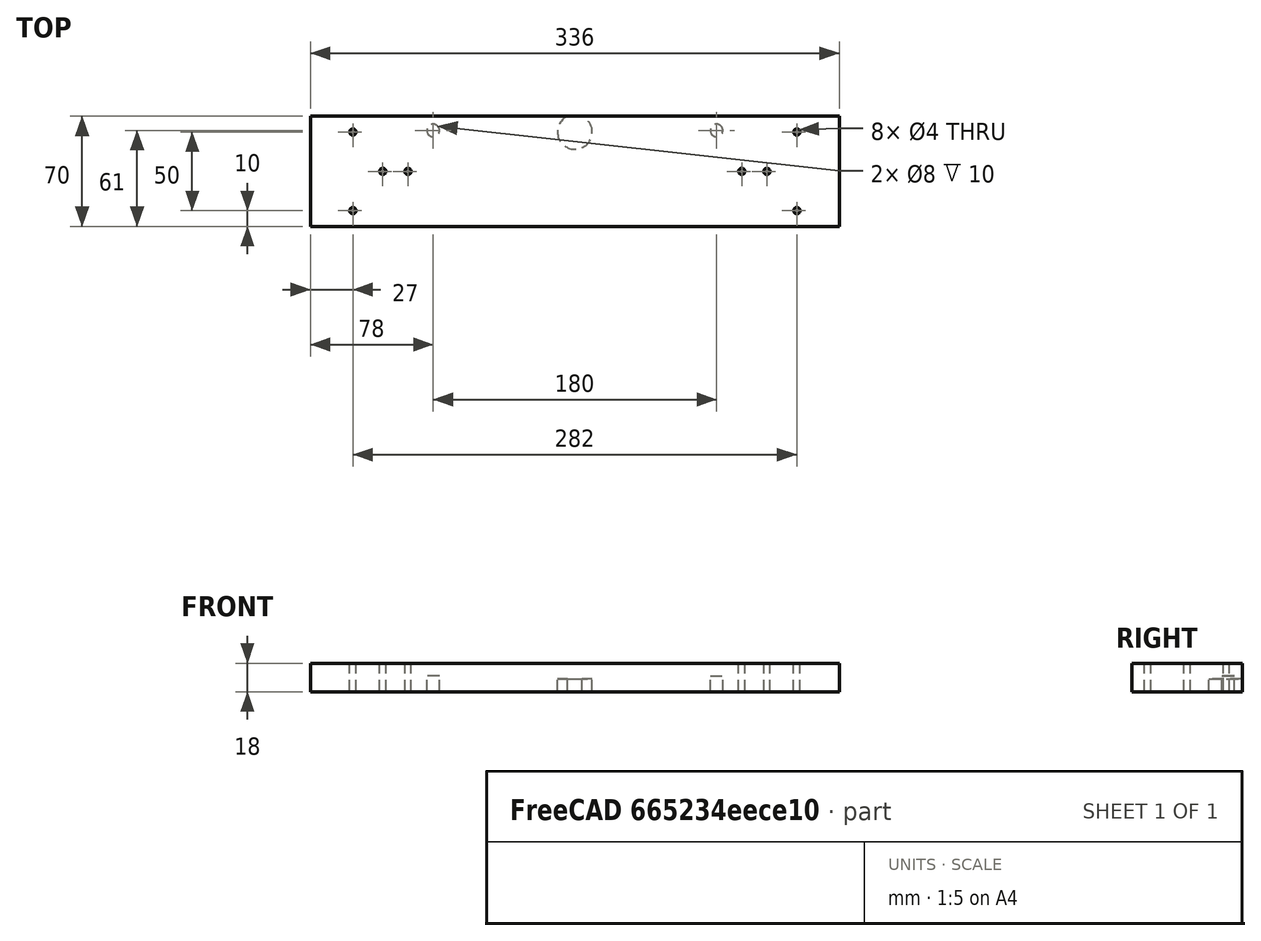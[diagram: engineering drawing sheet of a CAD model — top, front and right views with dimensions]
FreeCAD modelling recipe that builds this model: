
FCSTD DOCUMENT  (FreeCAD 0.17R13541 (Git))
Label: Base-Atras
License: All rights reserved
LicenseURL: http://en.wikipedia.org/wiki/All_rights_reserved
objects: Part::Cylinder×6, Part::MultiFuse×2, Part::Cut×2, Part::Box×1, Part::Mirroring×1
note: 12 computed .brp shape members not serialized (recipe doc carries the construction recipe); baked Part::Feature solids carry a one-line shape summary decoded from their .brp

FEATURE [Part::Box] Box  label="Base"
  AttacherType = Attacher::AttachEngine3D
  Height = 18
  Length = 168
  Width = 70
FEATURE [Part::Cylinder] Cylinder  label="Cilindro"
  Angle = 360
  AttacherType = Attacher::AttachEngine3D
  Height = 25
  Placement = pos=(27,10,0) rot=(0,0,1;0rad)
  Radius = 2
FEATURE [Part::Cylinder] Cylinder001  label="Cilindro001"
  Angle = 360
  AttacherType = Attacher::AttachEngine3D
  Height = 25
  Placement = pos=(27,60,0) rot=(0,0,1;0rad)
  Radius = 2
FEATURE [Part::Cylinder] Cylinder002  label="Cilindro002"
  Angle = 360
  AttacherType = Attacher::AttachEngine3D
  Height = 25
  Placement = pos=(46,35,0) rot=(0,0,1;0rad)
  Radius = 2
FEATURE [Part::Cylinder] Cylinder003  label="Cilindro003"
  Angle = 360
  AttacherType = Attacher::AttachEngine3D
  Height = 25
  Placement = pos=(62,35,0) rot=(0,0,1;0rad)
  Radius = 2
FEATURE [Part::Cylinder] Cylinder004  label="Cilindro004"
  Angle = 360
  AttacherType = Attacher::AttachEngine3D
  Height = 10
  Placement = pos=(78,61,0) rot=(0,0,1;0rad)
  Radius = 4
FEATURE [Part::Cylinder] Cylinder005  label="Cilindro005"
  Angle = 360
  AttacherType = Attacher::AttachEngine3D
  Height = 8
  Placement = pos=(168,60,0) rot=(0,0,1;0rad)
  Radius = 11
FEATURE [Part::MultiFuse] Fusion
  Refine = true
  Shapes = -> [Cylinder003,Cylinder004,Cylinder002,Cylinder001,Cylinder]
FEATURE [Part::Cut] Cut
  Base = -> Box
  Refine = true
  Tool = -> Fusion
FEATURE [Part::Mirroring] mirror  label="Mirror of Cut"
  Base = (168,0,0)
  Normal = (0.8,0,0)
  Source = -> Cut
FEATURE [Part::MultiFuse] Fusion001
  Refine = true
  Shapes = -> [mirror,Cut]
FEATURE [Part::Cut] Cut001
  Base = -> Fusion001
  Refine = true
  Tool = -> Cylinder005
